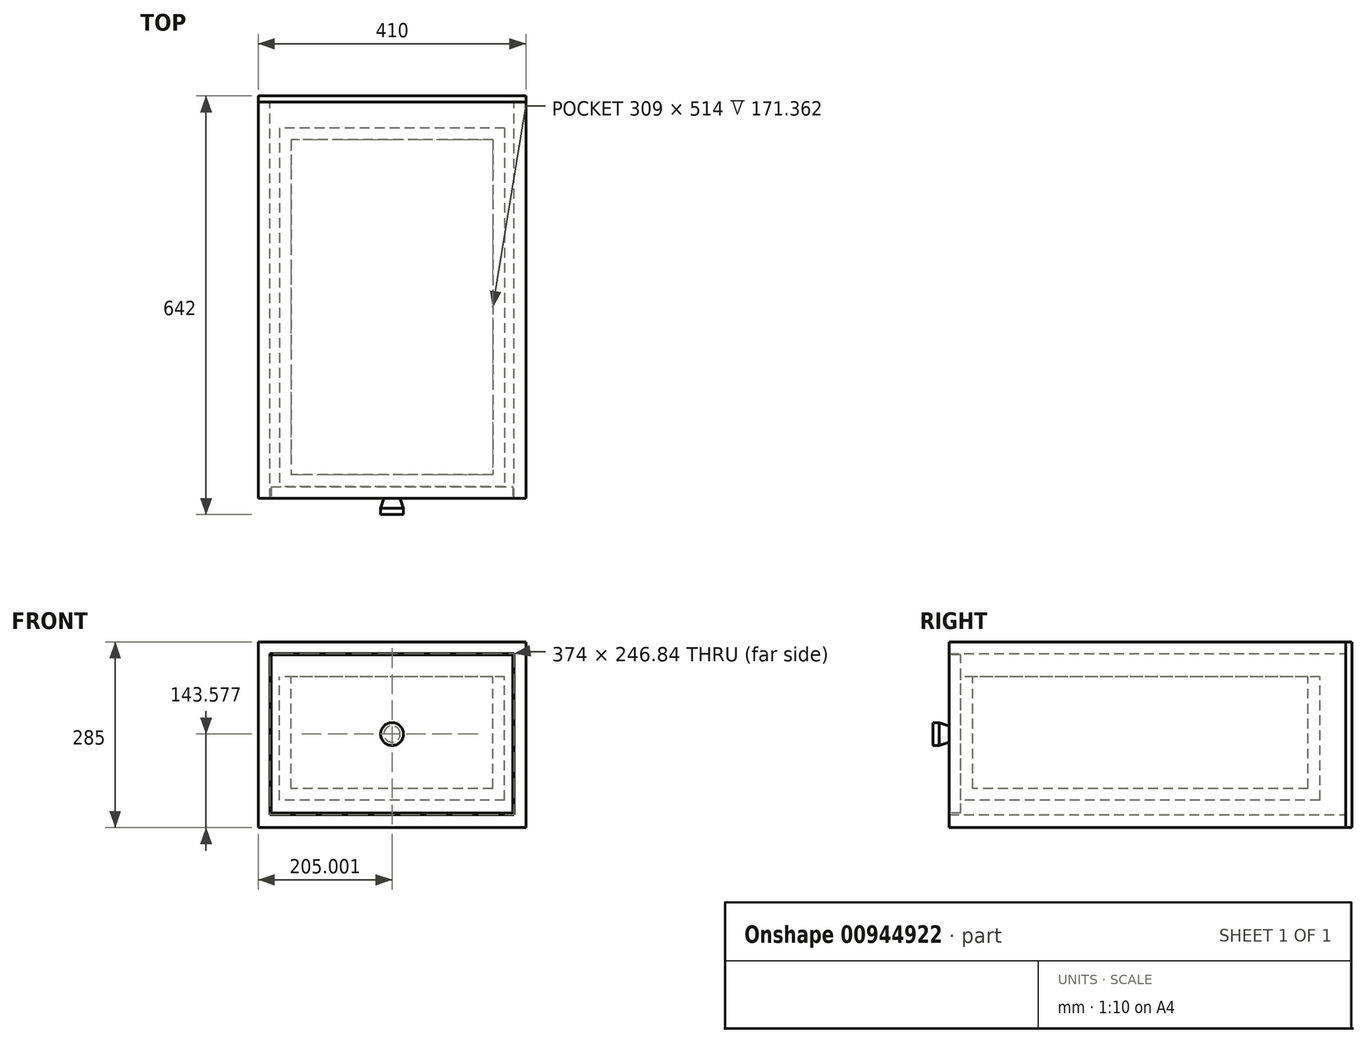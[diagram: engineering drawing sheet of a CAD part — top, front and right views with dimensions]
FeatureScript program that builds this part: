
annotation { "Feature Type Name" : "Feature", "Feature Type Description" : "" }
export const myFeature = defineFeature(function(context is Context, id is Id, definition is map)
    precondition{}
    {
        {
            var Q0;
            Q0=qCreatedBy(makeId("Front.planeOp"),FACE);
            var sketch = newSketch(context, id + "F0", { "sketchPlane" : qUnion([Q0])});
            skLineSegment(sketch, "E0", {"start": v(-326.85, -71.54) * mm, "end": v(-326.85, 213.46) * mm});
            skLineSegment(sketch, "E1.1", {"start": v(-308.85, -51.38) * mm, "end": v(-308.85, 195.46) * mm});
            skLineSegment(sketch, "E2.trimOffspring", {"start": v(65.15, -51.38) * mm, "end": v(-308.85, -51.38) * mm});
            skLineSegment(sketch, "E3.top", {"start": v(-308.85, 195.46) * mm, "end": v(65.15, 195.46) * mm});
            skLineSegment(sketch, "E4.trimOffspring", {"start": v(65.15, 195.46) * mm, "end": v(65.15, -51.38) * mm});
            skLineSegment(sketch, "E5", {"start": v(-326.85, 213.46) * mm, "end": v(83.15, 213.46) * mm});
            skLineSegment(sketch, "E6", {"start": v(83.15, -71.54) * mm, "end": v(83.15, 213.46) * mm});
            skLineSegment(sketch, "E7", {"start": v(-326.85, -71.54) * mm, "end": v(83.15, -71.54) * mm});
            skLineSegment(sketch, "E8.bottom", {"start": v(-326.85, 213.46) * mm, "end": v(303.15, 213.46) * mm, "construction": true});
            skLineSegment(sketch, "E9.left", {"start": v(83.15, 213.46) * mm, "end": v(83.15, -51.54) * mm, "construction": true});
            skSolve(sketch);
        }
        {
            var Q0;
            Q0=qSketchRegion(id+"F0",true);
            extrude(context, id + "F1", {"entities" : qUnion([Q0]), "depth" : 608 * mm, "offsetDistance" : 25 * mm});
        }
        {
            var Q0;
            Q0=makeQuery(id+"F1.opExtrude","CAP_FACE",FACE,{"disambiguationData":[OSD([sQuery(id+"F0.wireOp",EDGE,"E0"),sQuery(id+"F0.wireOp",EDGE,"1bbb11d5-5f90-4ef2-9ceb-a32cb31813a0"),sQuery(id+"F0.wireOp",EDGE,"E1.1"),sQuery(id+"F0.wireOp",EDGE,"E2.trimOffspring"),sQuery(id+"F0.wireOp",EDGE,"E3.top"),sQuery(id+"F0.wireOp",EDGE,"E4.trimOffspring"),sQuery(id+"F0.wireOp",EDGE,"E5"),sQuery(id+"F0.wireOp",EDGE,"E6")])],"isStart":true});
            var sketch = newSketch(context, id + "F2", { "sketchPlane" : qUnion([Q0])});
            skLineSegment(sketch, "E10.left", {"start": v(-83.15, 213.46) * mm, "end": v(-83.15, 213.46) * mm});
            skLineSegment(sketch, "E10.right", {"start": v(326.85, 213.46) * mm, "end": v(326.85, 213.46) * mm});
            skLineSegment(sketch, "E11.bottom", {"start": v(-83.15, 213.46) * mm, "end": v(326.85, 213.46) * mm});
            skLineSegment(sketch, "E11.top", {"start": v(-83.15, -71.54) * mm, "end": v(326.85, -71.54) * mm});
            skLineSegment(sketch, "E11.left", {"start": v(-83.15, 213.46) * mm, "end": v(-83.15, -71.54) * mm});
            skLineSegment(sketch, "E11.right", {"start": v(326.85, 213.46) * mm, "end": v(326.85, -71.54) * mm});
            skSolve(sketch);
        }
        {
            var Q0;
            Q0=qSketchRegion(id+"F2",true);
            extrude(context, id + "F3", {"entities" : qUnion([Q0]), "depth" : 9 * mm, "offsetDistance" : 25 * mm});
        }
        {
            var Q0;
            Q0=makeQuery(id+"F1.opExtrude","CAP_FACE",FACE,{"disambiguationData":[OSD([sQuery(id+"F0.wireOp",EDGE,"E0"),sQuery(id+"F0.wireOp",EDGE,"1bbb11d5-5f90-4ef2-9ceb-a32cb31813a0"),sQuery(id+"F0.wireOp",EDGE,"E1.1"),sQuery(id+"F0.wireOp",EDGE,"E2.trimOffspring"),sQuery(id+"F0.wireOp",EDGE,"E3.top"),sQuery(id+"F0.wireOp",EDGE,"E4.trimOffspring"),sQuery(id+"F0.wireOp",EDGE,"E5"),sQuery(id+"F0.wireOp",EDGE,"E6")])],"isStart":false});
            var sketch = newSketch(context, id + "F4", { "sketchPlane" : qUnion([Q0])});
            skLineSegment(sketch, "E12.0", {"start": v(-306.85, 193.46) * mm, "end": v(63.15, 193.46) * mm});
            skLineSegment(sketch, "E12.1", {"start": v(-306.85, -49.38) * mm, "end": v(-306.85, 193.46) * mm});
            skLineSegment(sketch, "E12.2", {"start": v(63.15, -49.38) * mm, "end": v(-306.85, -49.38) * mm});
            skLineSegment(sketch, "E12.3", {"start": v(63.15, 193.46) * mm, "end": v(63.15, -49.38) * mm});
            skSolve(sketch);
        }
        {
            var Q0;
            Q0=qSketchRegion(id+"F4",true);
            extrude(context, id + "F5", {"entities" : qUnion([Q0]), "oppositeDirection" : true, "depth" : 18 * mm, "offsetDistance" : 25 * mm});
        }
        {
            var Q0;
            Q0=makeQuery(id+"F5.opExtrude","CAP_FACE",FACE,{"disambiguationData":[OSD([sQuery(id+"F4.wireOp",EDGE,"E12.0"),sQuery(id+"F4.wireOp",EDGE,"E12.1"),sQuery(id+"F4.wireOp",EDGE,"E12.2"),sQuery(id+"F4.wireOp",EDGE,"E12.3")])],"isStart":false});
            var sketch = newSketch(context, id + "F6", { "sketchPlane" : qUnion([Q0])});
            skLineSegment(sketch, "E13.bottom", {"start": v(-50.65, -29.38) * mm, "end": v(294.35, -29.38) * mm});
            skLineSegment(sketch, "E13.top", {"start": v(-50.65, 159.98) * mm, "end": v(294.35, 159.98) * mm});
            skLineSegment(sketch, "E13.left", {"start": v(-50.65, -29.38) * mm, "end": v(-50.65, 159.98) * mm});
            skLineSegment(sketch, "E13.right", {"start": v(294.35, -29.38) * mm, "end": v(294.35, 159.98) * mm});
            skSolve(sketch);
        }
        {
            var Q0;
            Q0=qSketchRegion(id+"F6",true);
            extrude(context, id + "F7", {"entities" : qUnion([Q0]), "depth" : 550 * mm, "offsetDistance" : 25 * mm});
        }
        {
            var Q0;
            Q0=makeQuery(id+"F7.opExtrude","SWEPT_FACE",FACE,{"disambiguationData":[OSD([sQuery(id+"F6.wireOp",EDGE,"E13.top")])]});
            shell(context, id + "F8", {"entities" : qUnion([Q0]), "thickness" : 18 * mm});
        }
        {
            var Q0;
            Q0=makeQuery(id+"F5.opExtrude","CAP_FACE",FACE,{"disambiguationData":[OSD([sQuery(id+"F4.wireOp",EDGE,"E12.0"),sQuery(id+"F4.wireOp",EDGE,"E12.1"),sQuery(id+"F4.wireOp",EDGE,"E12.2"),sQuery(id+"F4.wireOp",EDGE,"E12.3")])],"isStart":true});
            var sketch = newSketch(context, id + "F9", { "sketchPlane" : qUnion([Q0])});
            skLineSegment(sketch, "E14", {"start": v(63.15, 72.04) * mm, "end": v(-306.85, 72.04) * mm, "construction": true});
            skCircle(sketch, "E15", {"center": v(-121.85, 72.04) * mm, "radius": 17.5 * mm});
            skSolve(sketch);
        }
        {
            var Q0;
            Q0=qSketchRegion(id+"F9",true);
            extrude(context, id + "F10", {"entities" : qUnion([Q0]), "depth" : 25 * mm, "offsetDistance" : 25 * mm});
        }
        {
            var Q0;
            Q0=makeQuery(id+"F10.opExtrude","CAP_EDGE",EDGE,{"disambiguationData":[OSD([sQuery(id+"F9.wireOp",EDGE,"E15")])],"isStart":true});
            chamfer(context, id + "F11", {"entities" : qUnion([Q0]), "chamferType" : ChamferType.TWO_OFFSETS, "width1" : 15 * mm, "oppositeDirection" : false, "width2" : 5 * mm, "tangentPropagation" : true});
        }
    });
